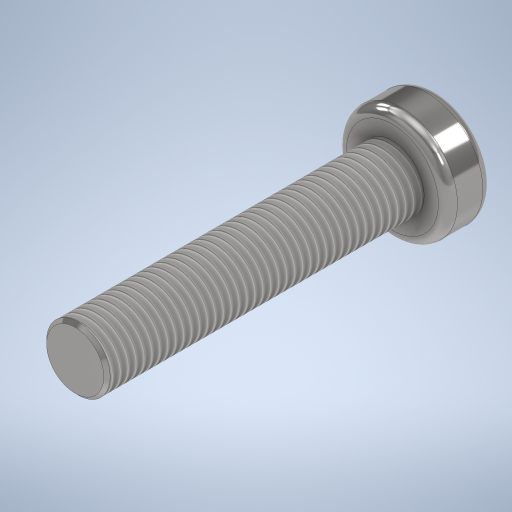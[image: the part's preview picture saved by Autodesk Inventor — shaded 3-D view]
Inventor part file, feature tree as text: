
AUTODESK INVENTOR PART (.ipt)
format: ipt  version: 2023.1 (Build 271208000, 208)  size: 343,552 bytes
history: native  units: mm
features: extrude x3, other x2, sketch x2, fillet x1, chamfer x1
ambient origin geometry x8: Origin, YZ Plane, XZ Plane, XY Plane, X Axis, Y Axis, Z Axis, Center Point
bodies: Body1 (feature_tree)
feature tree (9):
  other  "솔리드1"
  sketch  "스케치1"
  extrude  "돌출1"  Depth=2.0mm
  extrude  "돌출2"  Depth=10.0mm TaperAngle=0.0deg
  fillet  "모깎기1"  Radius=3.5mm
  extrude  "돌출3"  Depth=1.4mm TaperAngle=0.0deg
  chamfer  "모따기1"  Distance=0.3mm
  other  "스레드1"
  sketch  "스케치2"
